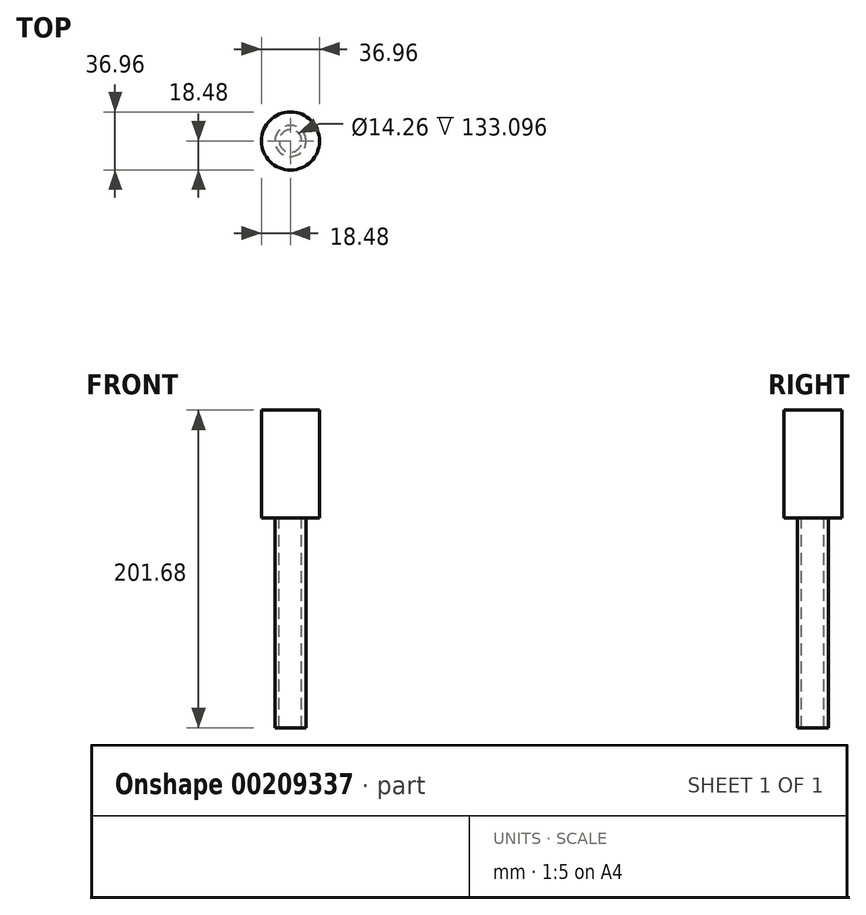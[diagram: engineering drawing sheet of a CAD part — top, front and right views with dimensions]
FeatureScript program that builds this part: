
annotation { "Feature Type Name" : "Feature", "Feature Type Description" : "" }
export const myFeature = defineFeature(function(context is Context, id is Id, definition is map)
    precondition{}
    {
        {
            var Q0;
            Q0=qCreatedBy(makeId("Top.planeOp"),FACE);
            var sketch = newSketch(context, id + "F0", { "sketchPlane" : qUnion([Q0])});
            skCircle(sketch, "E0", {"center": v(0, 0) * mm, "radius": 18.48 * mm});
            skSolve(sketch);
        }
        {
            var Q0;
            Q0=makeQuery(id+"F0.imprint","IMPRINT",FACE,{"disambiguationData":[TD([[makeQuery(id+"F0.imprint","IMPRINT",EDGE,{"derivedFrom":sQuery(id+"F0.wireOp",EDGE,"E0")}),1.0]])]});
            extrude(context, id + "F1", {"entities" : qUnion([Q0]), "depth" : 68.58 * mm});
        }
        {
            var Q0;
            Q0=makeQuery(id+"F1.opExtrude","CAP_FACE",FACE,{"disambiguationData":[OSD([sQuery(id+"F0.wireOp",EDGE,"E0")])],"isStart":false});
            var sketch = newSketch(context, id + "F2", { "sketchPlane" : qUnion([Q0])});
            skCircle(sketch, "E1", {"center": v(0, 0) * mm, "radius": 5.52 * mm});
            skCircle(sketch, "E2", {"center": v(0, 0) * mm, "radius": 7.13 * mm});
            skCircle(sketch, "E3", {"center": v(0, 0) * mm, "radius": 9.87 * mm});
            skSolve(sketch);
        }
        {
            var Q0;
            Q0=makeQuery(id+"F2.imprint","IMPRINT",FACE,{"disambiguationData":[TD([[makeQuery(id+"F2.imprint","IMPRINT",EDGE,{"derivedFrom":sQuery(id+"F2.wireOp",EDGE,"E2")}),-1.0]])]});
            extrude(context, id + "F3", {"entities" : qUnion([Q0]), "operationType" : NewBodyOperationType.ADD, "oppositeDirection" : true, "depth" : 201.68 * mm});
        }
    });
